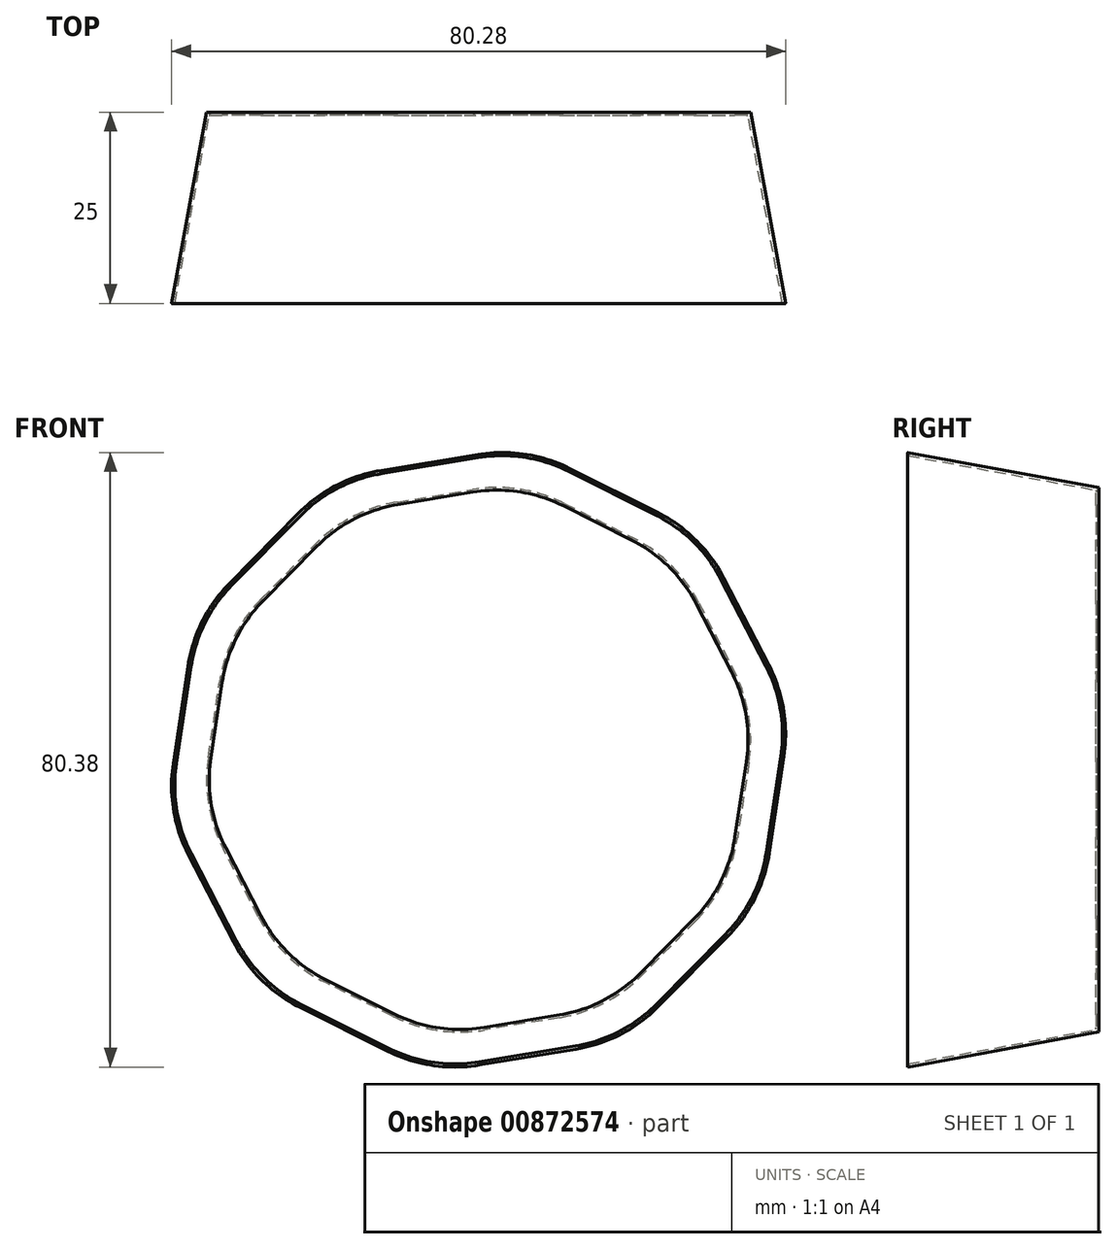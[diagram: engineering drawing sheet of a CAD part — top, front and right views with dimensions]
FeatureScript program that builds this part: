
annotation { "Feature Type Name" : "Feature", "Feature Type Description" : "" }
export const myFeature = defineFeature(function(context is Context, id is Id, definition is map)
    precondition{}
    {
        {
            var Q0;
            Q0=qCreatedBy(makeId("Front.planeOp"),FACE);
            var sketch = newSketch(context, id + "F0", { "sketchPlane" : qUnion([Q0])});
            skCircle(sketch, "E0.cCircle", {"center": v(0, 0) * mm, "radius": 35 * mm, "construction": true});
            skLineSegment(sketch, "E0.0", {"start": v(32.9, -16.48) * mm, "end": v(16.93, -32.67) * mm});
            skLineSegment(sketch, "E0.1", {"start": v(16.93, -32.67) * mm, "end": v(-5.5, -36.39) * mm});
            skLineSegment(sketch, "E0.2", {"start": v(-5.5, -36.39) * mm, "end": v(-25.84, -26.2) * mm});
            skLineSegment(sketch, "E0.3", {"start": v(-25.84, -26.2) * mm, "end": v(-36.3, -6) * mm});
            skLineSegment(sketch, "E0.4", {"start": v(-36.3, -6) * mm, "end": v(-32.9, 16.48) * mm});
            skLineSegment(sketch, "E0.5", {"start": v(-32.9, 16.48) * mm, "end": v(-16.93, 32.67) * mm});
            skLineSegment(sketch, "E0.6", {"start": v(-16.93, 32.67) * mm, "end": v(5.5, 36.39) * mm});
            skLineSegment(sketch, "E0.7", {"start": v(5.5, 36.39) * mm, "end": v(25.84, 26.2) * mm});
            skLineSegment(sketch, "E0.8", {"start": v(25.84, 26.2) * mm, "end": v(36.3, 6) * mm});
            skLineSegment(sketch, "E0.9", {"start": v(36.3, 6) * mm, "end": v(32.9, -16.48) * mm});
            skPoint(sketch, "E0.0.midPoint", {"position": v(24.92, -24.58) * mm});
            skSolve(sketch);
        }
        {
            var Q0;
            Q0=makeQuery(id+"F0.imprint","IMPRINT",FACE,{"disambiguationData":[TD([[makeQuery(id+"F0.imprint","IMPRINT",EDGE,{"derivedFrom":sQuery(id+"F0.wireOp",EDGE,"E0.0")}),-1.0]])]});
            extrude(context, id + "F1", {"entities" : qUnion([Q0]), "depth" : 25 * mm, "offsetDistance" : 25 * mm, "hasDraft" : true, "draftAngle" : 10 * degree});
        }
        {
            var Q0;
            Q0=makeQuery(id+"F1.opExtrude","SWEPT_EDGE",EDGE,{"disambiguationData":[OSD([sQuery(id+"F0.wireOp",EDGE,"E0.1"),sQuery(id+"F0.wireOp",EDGE,"E0.2")])]});
            var Q1;
            Q1=makeQuery(id+"F1.opExtrude","SWEPT_EDGE",EDGE,{"disambiguationData":[OSD([sQuery(id+"F0.wireOp",EDGE,"E0.2"),sQuery(id+"F0.wireOp",EDGE,"E0.3")])]});
            var Q2;
            Q2=makeQuery(id+"F1.opExtrude","SWEPT_EDGE",EDGE,{"disambiguationData":[OSD([sQuery(id+"F0.wireOp",EDGE,"E0.0"),sQuery(id+"F0.wireOp",EDGE,"E0.1")])]});
            var Q3;
            Q3=makeQuery(id+"F1.opExtrude","SWEPT_EDGE",EDGE,{"disambiguationData":[OSD([sQuery(id+"F0.wireOp",EDGE,"E0.0"),sQuery(id+"F0.wireOp",EDGE,"E0.9")])]});
            var Q4;
            Q4=makeQuery(id+"F1.opExtrude","SWEPT_EDGE",EDGE,{"disambiguationData":[OSD([sQuery(id+"F0.wireOp",EDGE,"E0.8"),sQuery(id+"F0.wireOp",EDGE,"E0.9")])]});
            var Q5;
            Q5=makeQuery(id+"F1.opExtrude","SWEPT_EDGE",EDGE,{"disambiguationData":[OSD([sQuery(id+"F0.wireOp",EDGE,"E0.7"),sQuery(id+"F0.wireOp",EDGE,"E0.8")])]});
            var Q6;
            Q6=makeQuery(id+"F1.opExtrude","SWEPT_EDGE",EDGE,{"disambiguationData":[OSD([sQuery(id+"F0.wireOp",EDGE,"E0.6"),sQuery(id+"F0.wireOp",EDGE,"E0.7")])]});
            var Q7;
            Q7=makeQuery(id+"F1.opExtrude","SWEPT_EDGE",EDGE,{"disambiguationData":[OSD([sQuery(id+"F0.wireOp",EDGE,"E0.5"),sQuery(id+"F0.wireOp",EDGE,"E0.6")])]});
            var Q8;
            Q8=makeQuery(id+"F1.opExtrude","SWEPT_EDGE",EDGE,{"disambiguationData":[OSD([sQuery(id+"F0.wireOp",EDGE,"E0.4"),sQuery(id+"F0.wireOp",EDGE,"E0.5")])]});
            var Q9;
            Q9=makeQuery(id+"F1.opExtrude","SWEPT_EDGE",EDGE,{"disambiguationData":[OSD([sQuery(id+"F0.wireOp",EDGE,"E0.3"),sQuery(id+"F0.wireOp",EDGE,"E0.4")])]});
            fillet(context, id + "F2", {"entities" : qUnion([Q0, Q1, Q2, Q3, Q4, Q5, Q6, Q7, Q8, Q9]), "radius" : 20 * mm, "tangentPropagation" : true, "allowEdgeOverflow" : false});
        }
        {
            var Q0;
            Q0=makeQuery(id+"F1.opExtrude","CAP_FACE",FACE,{"disambiguationData":[OSD([sQuery(id+"F0.wireOp",EDGE,"E0.0"),sQuery(id+"F0.wireOp",EDGE,"E0.1"),sQuery(id+"F0.wireOp",EDGE,"E0.2"),sQuery(id+"F0.wireOp",EDGE,"E0.3"),sQuery(id+"F0.wireOp",EDGE,"E0.4"),sQuery(id+"F0.wireOp",EDGE,"E0.5"),sQuery(id+"F0.wireOp",EDGE,"E0.6"),sQuery(id+"F0.wireOp",EDGE,"E0.7"),sQuery(id+"F0.wireOp",EDGE,"E0.8"),sQuery(id+"F0.wireOp",EDGE,"E0.9")])],"isStart":false});
            shell(context, id + "F3", {"entities" : qUnion([Q0]), "thickness" : 0.4 * mm});
        }
    });
